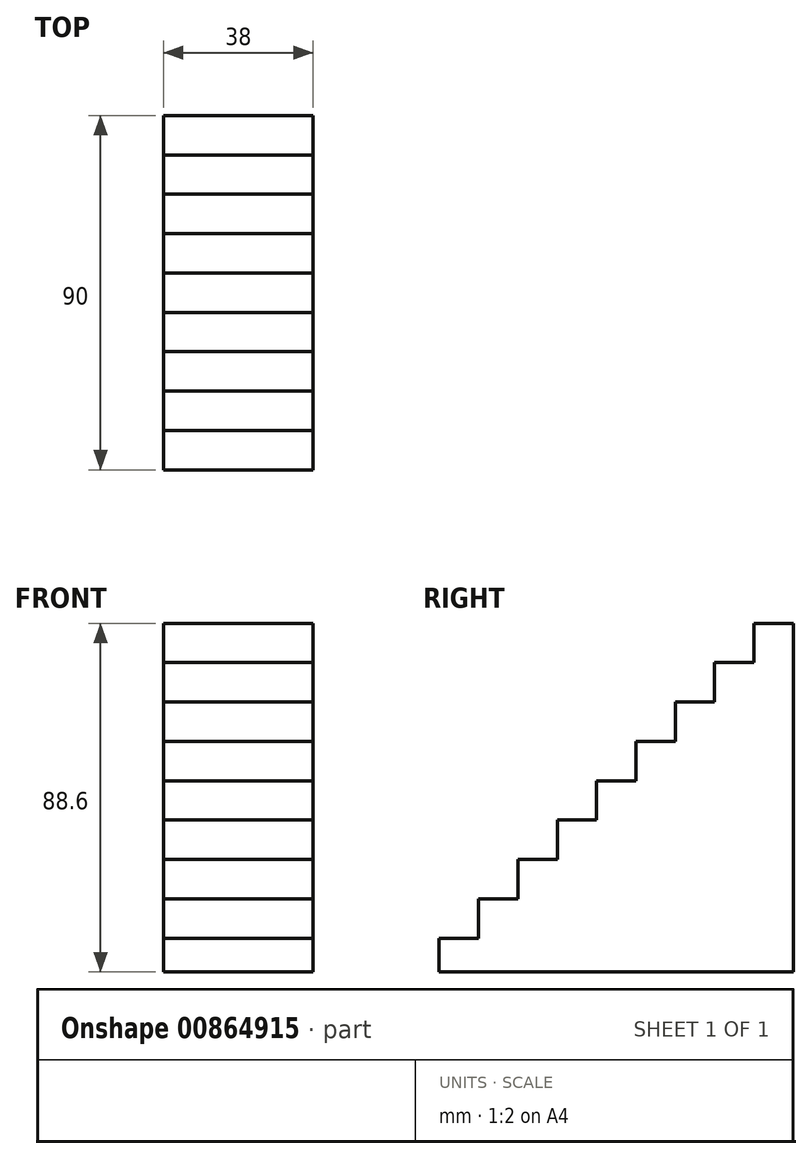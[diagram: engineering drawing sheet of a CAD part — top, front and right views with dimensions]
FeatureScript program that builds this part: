
annotation { "Feature Type Name" : "Feature", "Feature Type Description" : "" }
export const myFeature = defineFeature(function(context is Context, id is Id, definition is map)
    precondition{}
    {
        {
            var Q0;
            Q0=qCreatedBy(makeId("Front.planeOp"),FACE);
            var sketch = newSketch(context, id + "F0", { "sketchPlane" : qUnion([Q0])});
            skLineSegment(sketch, "E0.bottom", {"start": v(19, -44.3) * mm, "end": v(-19, -44.3) * mm});
            skLineSegment(sketch, "E0.top", {"start": v(19, 44.3) * mm, "end": v(-19, 44.3) * mm});
            skLineSegment(sketch, "E0.left", {"start": v(19, -44.3) * mm, "end": v(19, 44.3) * mm});
            skLineSegment(sketch, "E0.right", {"start": v(-19, -44.3) * mm, "end": v(-19, 44.3) * mm});
            skPoint(sketch, "E0.middle", {"position": v(0, 0) * mm});
            skSolve(sketch);
        }
        {
            var Q0;
            Q0=makeQuery(id+"F0.imprint","IMPRINT",FACE,{"disambiguationData":[TD([[makeQuery(id+"F0.imprint","IMPRINT",EDGE,{"derivedFrom":sQuery(id+"F0.wireOp",EDGE,"E0.bottom")}),-1.0]])]});
            extrude(context, id + "F1", {"entities" : qUnion([Q0]), "depth" : 10 * mm, "offsetDistance" : 25 * mm});
        }
        {
            var Q0;
            Q0=makeQuery(id+"F1.opExtrude","CAP_FACE",FACE,{"disambiguationData":[OSD([sQuery(id+"F0.wireOp",EDGE,"E0.bottom"),sQuery(id+"F0.wireOp",EDGE,"E0.top"),sQuery(id+"F0.wireOp",EDGE,"E0.left"),sQuery(id+"F0.wireOp",EDGE,"E0.right")])],"isStart":false});
            var sketch = newSketch(context, id + "F2", { "sketchPlane" : qUnion([Q0])});
            skLineSegment(sketch, "E1", {"start": v(-19, 44.3) * mm, "end": v(-19, 34.3) * mm, "construction": true});
            skLineSegment(sketch, "E2.bottom", {"start": v(-19, 34.3) * mm, "end": v(19, 34.3) * mm});
            skLineSegment(sketch, "E2.top", {"start": v(-19, 24.3) * mm, "end": v(19, 24.3) * mm});
            skLineSegment(sketch, "E2.left", {"start": v(-19, 34.3) * mm, "end": v(-19, 24.3) * mm});
            skLineSegment(sketch, "E2.right", {"start": v(19, 34.3) * mm, "end": v(19, 24.3) * mm});
            skSolve(sketch);
        }
        {
            var Q0;
            Q0=makeQuery(id+"F2.imprint","IMPRINT",FACE,{"disambiguationData":[TD([[makeQuery(id+"F2.imprint","IMPRINT",EDGE,{"derivedFrom":sQuery(id+"F2.wireOp",EDGE,"E2.bottom")}),-1.0]])]});
            extrude(context, id + "F3", {"entities" : qUnion([Q0]), "operationType" : NewBodyOperationType.ADD, "depth" : 10 * mm, "offsetDistance" : 25 * mm});
        }
        {
            var Q0;
            {var subQ0=sQuery(id+"F0.wireOp",EDGE,"E0.left");var subQ1=sQuery(id+"F0.wireOp",EDGE,"E0.right");var subQ2=sQuery(id+"F0.wireOp",EDGE,"E0.bottom");Q0=makeQuery(id+"F3.boolean.opBoolean","SPLIT",FACE,{"disambiguationData":[TD([makeQuery(id+"F1.opExtrude","SWEPT_FACE",FACE,{"disambiguationData":[OSD([subQ2])]})])],"derivedFrom":makeQuery(id+"F1.opExtrude","CAP_FACE",FACE,{"disambiguationData":[OSD([subQ2,sQuery(id+"F0.wireOp",EDGE,"E0.top"),subQ0,subQ1])],"isStart":false})});}
            var sketch = newSketch(context, id + "F4", { "sketchPlane" : qUnion([Q0])});
            skLineSegment(sketch, "E3.bottom", {"start": v(-19, 24.3) * mm, "end": v(19, 24.3) * mm});
            skLineSegment(sketch, "E3.top", {"start": v(-19, 14.3) * mm, "end": v(19, 14.3) * mm});
            skLineSegment(sketch, "E3.left", {"start": v(-19, 24.3) * mm, "end": v(-19, 14.3) * mm});
            skLineSegment(sketch, "E3.right", {"start": v(19, 24.3) * mm, "end": v(19, 14.3) * mm});
            skSolve(sketch);
        }
        {
            var Q0;
            Q0 = qSketchRegion(id + "F4", true);
            extrude(context, id + "F5", {"entities" : qUnion([Q0]), "operationType" : NewBodyOperationType.ADD, "depth" : 20 * mm, "offsetDistance" : 25 * mm});
        }
        {
            var Q0;
            {var subQ0=sQuery(id+"F0.wireOp",EDGE,"E0.left");var subQ1=sQuery(id+"F0.wireOp",EDGE,"E0.right");var subQ2=sQuery(id+"F0.wireOp",EDGE,"E0.bottom");Q0=makeQuery(id+"F3.boolean.opBoolean","SPLIT",FACE,{"disambiguationData":[TD([makeQuery(id+"F1.opExtrude","SWEPT_FACE",FACE,{"disambiguationData":[OSD([subQ2])]})])],"derivedFrom":makeQuery(id+"F1.opExtrude","CAP_FACE",FACE,{"disambiguationData":[OSD([subQ2,sQuery(id+"F0.wireOp",EDGE,"E0.top"),subQ0,subQ1])],"isStart":false})});}
            var sketch = newSketch(context, id + "F6", { "sketchPlane" : qUnion([Q0])});
            skLineSegment(sketch, "E4.bottom", {"start": v(-19, 14.3) * mm, "end": v(19, 14.3) * mm});
            skLineSegment(sketch, "E4.top", {"start": v(-19, 4.3) * mm, "end": v(19, 4.3) * mm});
            skLineSegment(sketch, "E4.left", {"start": v(-19, 14.3) * mm, "end": v(-19, 4.3) * mm});
            skLineSegment(sketch, "E4.right", {"start": v(19, 14.3) * mm, "end": v(19, 4.3) * mm});
            skSolve(sketch);
        }
        {
            var Q0;
            Q0 = qSketchRegion(id + "F6", true);
            extrude(context, id + "F7", {"entities" : qUnion([Q0]), "operationType" : NewBodyOperationType.ADD, "depth" : 30 * mm, "offsetDistance" : 25 * mm});
        }
        {
            var Q0;
            {var subQ0=sQuery(id+"F0.wireOp",EDGE,"E0.left");var subQ1=sQuery(id+"F0.wireOp",EDGE,"E0.right");var subQ2=sQuery(id+"F0.wireOp",EDGE,"E0.bottom");Q0=makeQuery(id+"F3.boolean.opBoolean","SPLIT",FACE,{"disambiguationData":[TD([makeQuery(id+"F1.opExtrude","SWEPT_FACE",FACE,{"disambiguationData":[OSD([subQ2])]})])],"derivedFrom":makeQuery(id+"F1.opExtrude","CAP_FACE",FACE,{"disambiguationData":[OSD([subQ2,sQuery(id+"F0.wireOp",EDGE,"E0.top"),subQ0,subQ1])],"isStart":false})});}
            var sketch = newSketch(context, id + "F8", { "sketchPlane" : qUnion([Q0])});
            skLineSegment(sketch, "E5.bottom", {"start": v(-19, 4.3) * mm, "end": v(19, 4.3) * mm});
            skLineSegment(sketch, "E5.top", {"start": v(-19, -5.7) * mm, "end": v(19, -5.7) * mm});
            skLineSegment(sketch, "E5.left", {"start": v(-19, 4.3) * mm, "end": v(-19, -5.7) * mm});
            skLineSegment(sketch, "E5.right", {"start": v(19, 4.3) * mm, "end": v(19, -5.7) * mm});
            skSolve(sketch);
        }
        {
            var Q0;
            Q0 = qSketchRegion(id + "F8", true);
            extrude(context, id + "F9", {"entities" : qUnion([Q0]), "operationType" : NewBodyOperationType.ADD, "depth" : 40 * mm, "offsetDistance" : 25 * mm});
        }
        {
            var Q0;
            {var subQ0=sQuery(id+"F0.wireOp",EDGE,"E0.left");var subQ1=sQuery(id+"F0.wireOp",EDGE,"E0.right");var subQ2=sQuery(id+"F0.wireOp",EDGE,"E0.bottom");Q0=makeQuery(id+"F3.boolean.opBoolean","SPLIT",FACE,{"disambiguationData":[TD([makeQuery(id+"F1.opExtrude","SWEPT_FACE",FACE,{"disambiguationData":[OSD([subQ2])]})])],"derivedFrom":makeQuery(id+"F1.opExtrude","CAP_FACE",FACE,{"disambiguationData":[OSD([subQ2,sQuery(id+"F0.wireOp",EDGE,"E0.top"),subQ0,subQ1])],"isStart":false})});}
            var sketch = newSketch(context, id + "F10", { "sketchPlane" : qUnion([Q0])});
            skLineSegment(sketch, "E6.bottom", {"start": v(-19, -5.7) * mm, "end": v(19, -5.7) * mm});
            skLineSegment(sketch, "E6.top", {"start": v(-19, -15.7) * mm, "end": v(19, -15.7) * mm});
            skLineSegment(sketch, "E6.left", {"start": v(-19, -5.7) * mm, "end": v(-19, -15.7) * mm});
            skLineSegment(sketch, "E6.right", {"start": v(19, -5.7) * mm, "end": v(19, -15.7) * mm});
            skSolve(sketch);
        }
        {
            var Q0;
            Q0 = qSketchRegion(id + "F10", true);
            extrude(context, id + "F11", {"entities" : qUnion([Q0]), "operationType" : NewBodyOperationType.ADD, "depth" : 50 * mm, "offsetDistance" : 25 * mm});
        }
        {
            var Q0;
            {var subQ0=sQuery(id+"F0.wireOp",EDGE,"E0.left");var subQ1=sQuery(id+"F0.wireOp",EDGE,"E0.right");var subQ2=sQuery(id+"F0.wireOp",EDGE,"E0.bottom");Q0=makeQuery(id+"F3.boolean.opBoolean","SPLIT",FACE,{"disambiguationData":[TD([makeQuery(id+"F1.opExtrude","SWEPT_FACE",FACE,{"disambiguationData":[OSD([subQ2])]})])],"derivedFrom":makeQuery(id+"F1.opExtrude","CAP_FACE",FACE,{"disambiguationData":[OSD([subQ2,sQuery(id+"F0.wireOp",EDGE,"E0.top"),subQ0,subQ1])],"isStart":false})});}
            var sketch = newSketch(context, id + "F12", { "sketchPlane" : qUnion([Q0])});
            skLineSegment(sketch, "E7.bottom", {"start": v(-19, -15.7) * mm, "end": v(19, -15.7) * mm});
            skLineSegment(sketch, "E7.top", {"start": v(-19, -25.7) * mm, "end": v(19, -25.7) * mm});
            skLineSegment(sketch, "E7.left", {"start": v(-19, -15.7) * mm, "end": v(-19, -25.7) * mm});
            skLineSegment(sketch, "E7.right", {"start": v(19, -15.7) * mm, "end": v(19, -25.7) * mm});
            skSolve(sketch);
        }
        {
            var Q0;
            Q0 = qSketchRegion(id + "F12", true);
            extrude(context, id + "F13", {"entities" : qUnion([Q0]), "operationType" : NewBodyOperationType.ADD, "depth" : 60 * mm, "offsetDistance" : 25 * mm});
        }
        {
            var Q0;
            {var subQ0=sQuery(id+"F0.wireOp",EDGE,"E0.left");var subQ1=sQuery(id+"F0.wireOp",EDGE,"E0.right");var subQ2=sQuery(id+"F0.wireOp",EDGE,"E0.bottom");Q0=makeQuery(id+"F3.boolean.opBoolean","SPLIT",FACE,{"disambiguationData":[TD([makeQuery(id+"F1.opExtrude","SWEPT_FACE",FACE,{"disambiguationData":[OSD([subQ2])]})])],"derivedFrom":makeQuery(id+"F1.opExtrude","CAP_FACE",FACE,{"disambiguationData":[OSD([subQ2,sQuery(id+"F0.wireOp",EDGE,"E0.top"),subQ0,subQ1])],"isStart":false})});}
            var sketch = newSketch(context, id + "F14", { "sketchPlane" : qUnion([Q0])});
            skLineSegment(sketch, "E8.bottom", {"start": v(-19, -25.7) * mm, "end": v(19, -25.7) * mm});
            skLineSegment(sketch, "E8.top", {"start": v(-19, -35.7) * mm, "end": v(19, -35.7) * mm});
            skLineSegment(sketch, "E8.left", {"start": v(-19, -25.7) * mm, "end": v(-19, -35.7) * mm});
            skLineSegment(sketch, "E8.right", {"start": v(19, -25.7) * mm, "end": v(19, -35.7) * mm});
            skSolve(sketch);
        }
        {
            var Q0;
            Q0 = qSketchRegion(id + "F14", true);
            extrude(context, id + "F15", {"entities" : qUnion([Q0]), "operationType" : NewBodyOperationType.ADD, "depth" : 70 * mm, "offsetDistance" : 25 * mm});
        }
        {
            var Q0;
            {var subQ0=sQuery(id+"F0.wireOp",EDGE,"E0.left");var subQ1=sQuery(id+"F0.wireOp",EDGE,"E0.right");var subQ2=sQuery(id+"F0.wireOp",EDGE,"E0.bottom");Q0=makeQuery(id+"F3.boolean.opBoolean","SPLIT",FACE,{"disambiguationData":[TD([makeQuery(id+"F1.opExtrude","SWEPT_FACE",FACE,{"disambiguationData":[OSD([subQ2])]})])],"derivedFrom":makeQuery(id+"F1.opExtrude","CAP_FACE",FACE,{"disambiguationData":[OSD([subQ2,sQuery(id+"F0.wireOp",EDGE,"E0.top"),subQ0,subQ1])],"isStart":false})});}
            var sketch = newSketch(context, id + "F16", { "sketchPlane" : qUnion([Q0])});
            skLineSegment(sketch, "E9.bottom", {"start": v(-19, -35.7) * mm, "end": v(19, -35.7) * mm});
            skLineSegment(sketch, "E9.top", {"start": v(-19, -44.3) * mm, "end": v(19, -44.3) * mm});
            skLineSegment(sketch, "E9.left", {"start": v(-19, -35.7) * mm, "end": v(-19, -44.3) * mm});
            skLineSegment(sketch, "E9.right", {"start": v(19, -35.7) * mm, "end": v(19, -44.3) * mm});
            skSolve(sketch);
        }
        {
            var Q0;
            Q0 = qSketchRegion(id + "F16", true);
            extrude(context, id + "F17", {"entities" : qUnion([Q0]), "operationType" : NewBodyOperationType.ADD, "depth" : 80 * mm, "offsetDistance" : 25 * mm});
        }
    });
